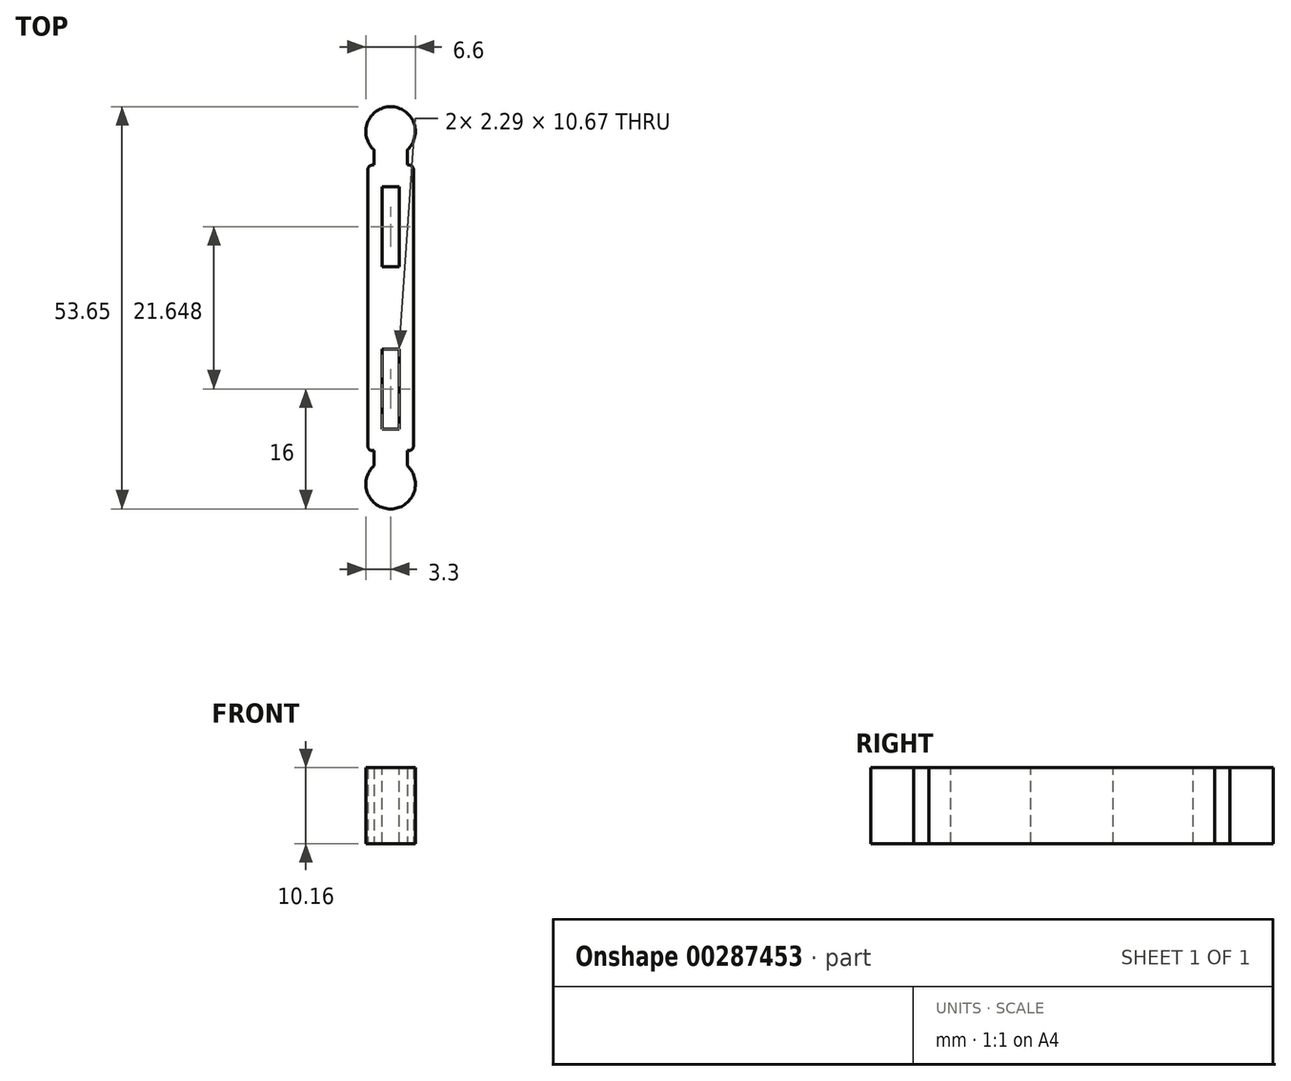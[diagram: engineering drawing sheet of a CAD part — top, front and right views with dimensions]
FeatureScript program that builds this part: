
annotation { "Feature Type Name" : "Feature", "Feature Type Description" : "" }
export const myFeature = defineFeature(function(context is Context, id is Id, definition is map)
    precondition{}
    {
        {
            var Q0;
            Q0=qCreatedBy(makeId("Top.planeOp"),FACE);
            var sketch = newSketch(context, id + "F0", { "sketchPlane" : qUnion([Q0])});
            skCircle(sketch, "E0", {"center": v(0, 0) * mm, "radius": 3.3 * mm});
            skSolve(sketch);
        }
        {
            var Q0;
            Q0 = qSketchRegion(id + "F0", true);
            extrude(context, id + "F1", {"entities" : qUnion([Q0]), "depth" : 10.16 * mm});
        }
        {
            var Q0;
            Q0=makeQuery(id+"F1.opExtrude","CAP_FACE",FACE,{"disambiguationData":[OSD([sQuery(id+"F0.wireOp",EDGE,"E0")])],"isStart":true});
            var sketch = newSketch(context, id + "F2", { "sketchPlane" : qUnion([Q0])});
            skLineSegment(sketch, "E1.bottom", {"start": v(-2.22, -2.44) * mm, "end": v(2.22, -2.44) * mm});
            skLineSegment(sketch, "E1.top", {"start": v(-2.22, -4.47) * mm, "end": v(2.22, -4.47) * mm});
            skLineSegment(sketch, "E1.left", {"start": v(-2.22, -2.44) * mm, "end": v(-2.22, -4.47) * mm});
            skLineSegment(sketch, "E1.right", {"start": v(2.22, -2.44) * mm, "end": v(2.22, -4.47) * mm});
            skSolve(sketch);
        }
        {
            var Q0;
            Q0=makeQuery(id+"F2.imprint","IMPRINT",FACE,{"disambiguationData":[TD([[makeQuery(id+"F2.imprint","IMPRINT",EDGE,{"derivedFrom":sQuery(id+"F2.wireOp",EDGE,"E1.top")}),1.0]])]});
            var Q1;
            Q1=makeQuery(id+"F1.opExtrude","CAP_FACE",FACE,{"disambiguationData":[OSD([sQuery(id+"F0.wireOp",EDGE,"E0")])],"isStart":false});
            extrude(context, id + "F3", {"entities" : qUnion([Q0]), "operationType" : NewBodyOperationType.ADD, "endBound" : BoundingType.UP_TO_SURFACE, "oppositeDirection" : true, "endBoundEntityFace" : qUnion([Q1]), "depth" : 25.4 * mm});
        }
        {
            var Q0;
            Q0=qCreatedBy(makeId("Top.planeOp"),FACE);
            var sketch = newSketch(context, id + "F4", { "sketchPlane" : qUnion([Q0])});
            skLineSegment(sketch, "E2.bottom", {"start": v(-3.05, 4.47) * mm, "end": v(3.05, 4.47) * mm});
            skLineSegment(sketch, "E2.top", {"start": v(-3.05, 23.52) * mm, "end": v(3.05, 23.52) * mm});
            skLineSegment(sketch, "E2.left", {"start": v(-3.05, 4.47) * mm, "end": v(-3.05, 23.52) * mm});
            skLineSegment(sketch, "E2.right", {"start": v(3.05, 4.47) * mm, "end": v(3.05, 23.52) * mm});
            skSolve(sketch);
        }
        {
            var Q0;
            Q0 = qSketchRegion(id + "F4", true);
            var Q1;
            {var subQ0=sQuery(id+"F0.wireOp",EDGE,"E0");Q1=makeQuery(id+"F3.boolean.opBoolean","MERGE",FACE,{"derivedFrom":[makeQuery(id+"F1.opExtrude","CAP_FACE",FACE,{"disambiguationData":[OSD([subQ0])],"isStart":false}),makeQuery(id+"F3.opExtrude","CAP_FACE",FACE,{"disambiguationData":[OSD([subQ0])],"isStart":false})]});}
            extrude(context, id + "F5", {"entities" : qUnion([Q0]), "operationType" : NewBodyOperationType.ADD, "endBound" : BoundingType.UP_TO_SURFACE, "endBoundEntityFace" : qUnion([Q1]), "depth" : 25.4 * mm});
        }
        {
            var Q0;
            Q0=makeQuery(id+"F5.opExtrude","SWEPT_EDGE",EDGE,{"disambiguationData":[OSD([sQuery(id+"F4.wireOp",EDGE,"E2.bottom"),sQuery(id+"F4.wireOp",EDGE,"E2.right")])]});
            var Q1;
            Q1=makeQuery(id+"F5.opExtrude","SWEPT_EDGE",EDGE,{"disambiguationData":[OSD([sQuery(id+"F4.wireOp",EDGE,"E2.bottom"),sQuery(id+"F4.wireOp",EDGE,"E2.left")])]});
            fillet(context, id + "F6", {"entities" : qUnion([Q0, Q1]), "radius" : 0.64 * mm, "tangentPropagation" : true, "allowEdgeOverflow" : false});
        }
        {
            var Q0;
            {var subQ0=sQuery(id+"F0.wireOp",EDGE,"E0");Q0=makeQuery(id+"F5.boolean.opBoolean","MERGE",FACE,{"derivedFrom":[makeQuery(id+"F3.boolean.opBoolean","MERGE",FACE,{"derivedFrom":[makeQuery(id+"F1.opExtrude","CAP_FACE",FACE,{"disambiguationData":[OSD([subQ0])],"isStart":false}),makeQuery(id+"F3.opExtrude","CAP_FACE",FACE,{"disambiguationData":[OSD([subQ0])],"isStart":false})]}),makeQuery(id+"F5.opExtrude","CAP_FACE",FACE,{"disambiguationData":[OSD([subQ0])],"isStart":false})]});}
            var sketch = newSketch(context, id + "F7", { "sketchPlane" : qUnion([Q0])});
            skLineSegment(sketch, "E3.bottom", {"start": v(1.14, 7.37) * mm, "end": v(-1.14, 7.37) * mm});
            skLineSegment(sketch, "E3.top", {"start": v(1.14, 18.03) * mm, "end": v(-1.14, 18.03) * mm});
            skLineSegment(sketch, "E3.left", {"start": v(1.14, 7.37) * mm, "end": v(1.14, 18.03) * mm});
            skLineSegment(sketch, "E3.right", {"start": v(-1.14, 7.37) * mm, "end": v(-1.14, 18.03) * mm});
            skPoint(sketch, "E3.middle", {"position": v(0, 12.7) * mm});
            skSolve(sketch);
        }
        {
            var Q0;
            Q0=makeQuery(id+"F7.imprint","IMPRINT",FACE,{"disambiguationData":[TD([[makeQuery(id+"F7.imprint","IMPRINT",EDGE,{"derivedFrom":sQuery(id+"F7.wireOp",EDGE,"E3.bottom")}),-1.0]])]});
            extrude(context, id + "F8", {"entities" : qUnion([Q0]), "operationType" : NewBodyOperationType.REMOVE, "oppositeDirection" : true, "depth" : 25.4 * mm});
        }
        {
            var Q0;
            Q0=makeQuery(id+"F1.opExtrude","SWEPT_BODY",BODY,{"disambiguationData":[OSD([sQuery(id+"F0.wireOp",EDGE,"E0")])]});
            var Q1;
            Q1=makeQuery(id+"F5.opExtrude","SWEPT_FACE",FACE,{"disambiguationData":[OSD([sQuery(id+"F4.wireOp",EDGE,"E2.top")])]});
            mirror(context, id + "F9", {"operationType" : NewBodyOperationType.ADD, "entities" : qUnion([Q0]), "mirrorPlane" : qUnion([Q1])});
        }
    });
